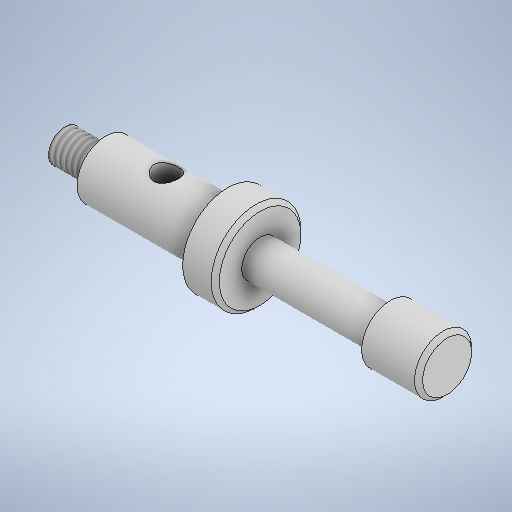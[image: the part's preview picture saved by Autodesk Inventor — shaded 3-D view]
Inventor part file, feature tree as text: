
AUTODESK INVENTOR PART (.ipt)
format: ipt  version: 2025.1 (Build 291241000, 241)  size: 320,512 bytes
history: native  units: mm
features: sketch x3, revolve x2, thread x1, chamfer x1, plane x1, hole x1
ambient origin geometry x8: Origin, YZ Plane, XZ Plane, XY Plane, X Axis, Y Axis, Z Axis, Center Point
bodies: Solid1 (feature_tree)
feature tree (9):
  revolve  "Revolution1"  [1 undecoded]
  thread  "Thread1"  [1 undecoded]
  chamfer  "Chamfer1"  Distance=7.0mm
  plane  "Work Plane1"
  hole  "Hole1"  [1 undecoded]
  revolve  "Revolution3"  [1 undecoded]
  sketch  "Sketch1"  dims[d0=4.0mm d1=7.0mm d2=5.0mm]
  sketch  "Sketch2"  dims[d3=15.0mm]
  sketch  "Sketch4"  dims[d4=47.0mm d5=7.0mm d6=16.0mm d7=4.5mm d8=4.0mm d10=11.0mm d11=90.0deg d12=10.0mm d13=0.0mm d14=0.5mm d15=2.0mm d16=45.0deg d17=3.5mm d18=7.5mm d19=3.0mm d20=8.0mm d21=4.0mm d22=2.0mm d23=90.0deg d24=8.0mm d25=20.594885mm d31=360.0deg d38=30.0deg]
note: 4 required parameter values undecoded (feature->parameter linkage not recoverable at this tier; creation-order binding heuristic only, values carry confidence <= 0.55)